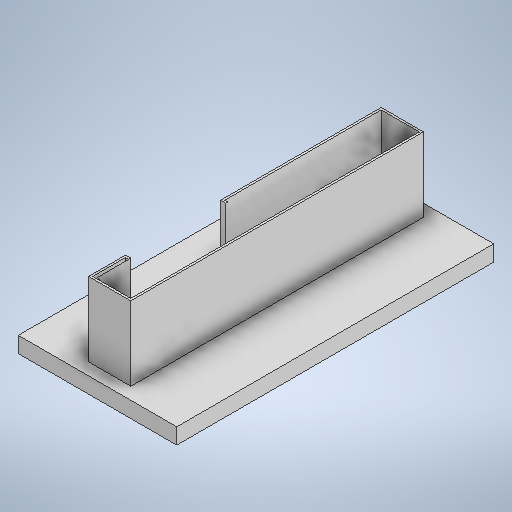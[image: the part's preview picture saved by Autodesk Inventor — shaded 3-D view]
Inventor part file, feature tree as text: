
AUTODESK INVENTOR PART (.ipt)
format: ipt  version: 2025.2 (Build 292293000, 293)  size: 443,392 bytes
history: native  units: mm
features: delete_face x4, extrude x3, sketch x2, shell x1, chamfer x1
ambient origin geometry x8: Origin, YZ Plane, XZ Plane, XY Plane, X Axis, Y Axis, Z Axis, Center Point
bodies: Solid1 (feature_tree), Solid2 (feature_tree)
feature tree (11):
  extrude  "Extrusion1"  Depth=300.0mm
  sketch  "Sketch2"  dims[d2=15.0mm d3=0.0mm d4=30.0mm d5=267.0mm d6=70.0mm d7=0.0mm d8=2.0mm d9=2.0mm d10=2.0mm d11=45.0deg d22=5.0mm d24=5.0mm d27=5.0mm d28=5.0mm d30=15.0mm d31=15.0mm d32=15.0mm d33=0.0mm d12=1.0mm d13=1.0mm d14=1.0mm d15=0.15mm d16=0.25mm d17=0.375mm d18=14.3117mm d19=0.75mm d20=20.594885mm d21=0.0625mm d23=0.375mm d29=0.5mm]
  extrude  "Extrusion2"  Depth=30.0mm
  shell  "Shell1"  Thickness=267.0mm
  chamfer  "Chamfer1"  Distance=70.0mm
  delete_face  "Delete Face1"
  delete_face  "Delete Face2"
  delete_face  "Delete Face3"
  delete_face  "Delete Face4"
  extrude  "Extrusion3"  Depth=2.0mm
  sketch  "Sketch1"  dims[d0=150.0mm d1=300.0mm]
